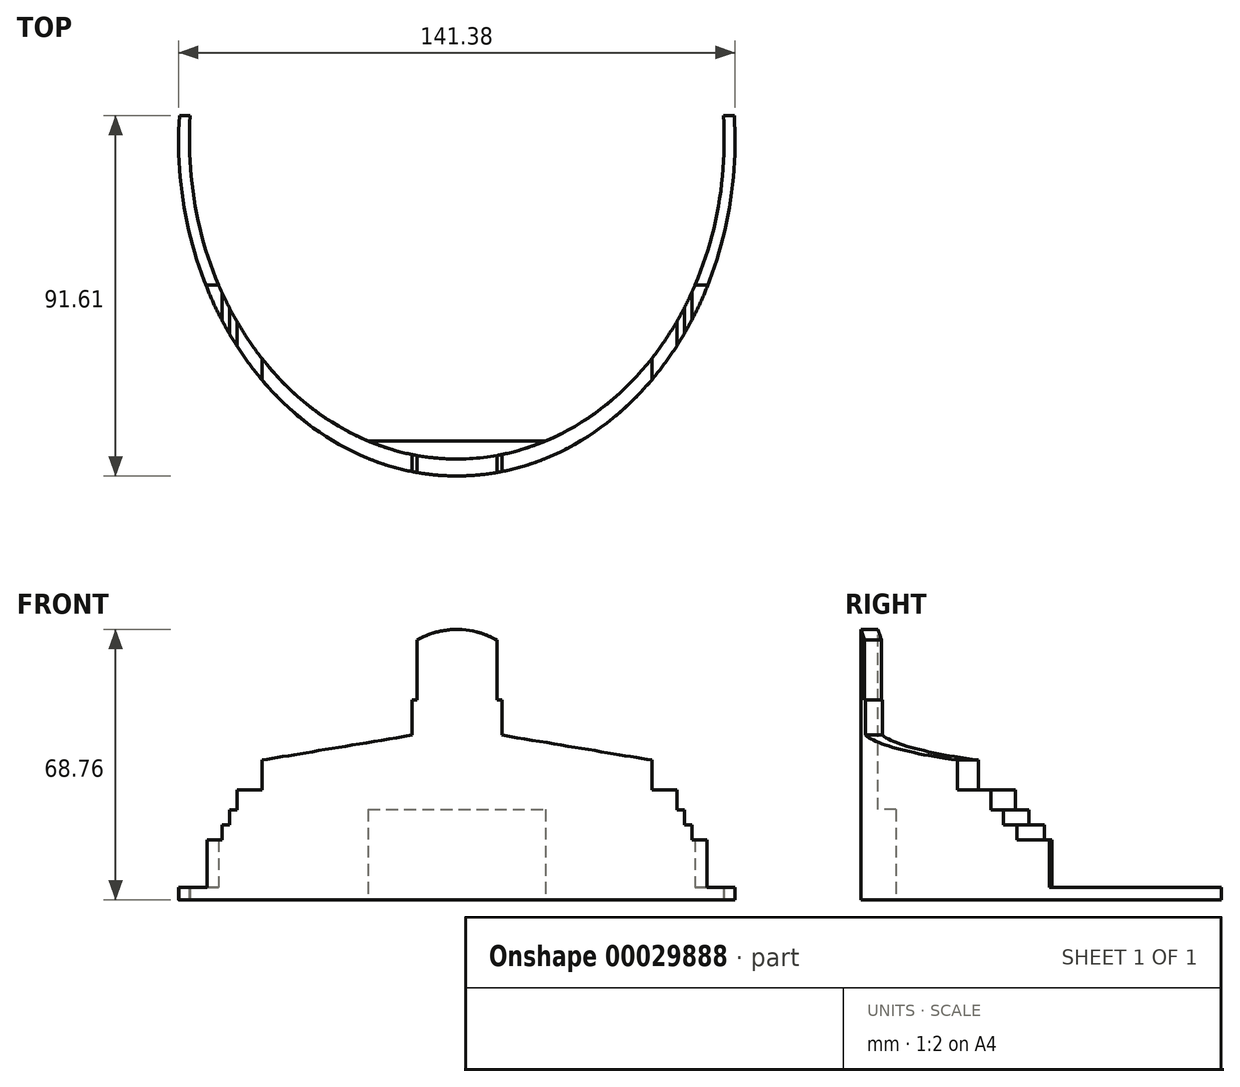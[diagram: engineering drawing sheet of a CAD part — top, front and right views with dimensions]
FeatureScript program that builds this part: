
annotation { "Feature Type Name" : "Feature", "Feature Type Description" : "" }
export const myFeature = defineFeature(function(context is Context, id is Id, definition is map)
    precondition{}
    {
        {
            var Q0;
            Q0=qCreatedBy(makeId("Front.planeOp"),FACE);
            var sketch = newSketch(context, id + "F0", { "sketchPlane" : qUnion([Q0])});
            skLineSegment(sketch, "E0", {"start": v(-63.5, 0) * mm, "end": v(63.5, 0) * mm});
            skLineSegment(sketch, "E1", {"start": v(63.5, 0) * mm, "end": v(63.5, 15.24) * mm});
            skLineSegment(sketch, "E2", {"start": v(63.5, 15.24) * mm, "end": v(59.69, 15.24) * mm});
            skLineSegment(sketch, "E3", {"start": v(59.69, 15.24) * mm, "end": v(59.69, 19.05) * mm});
            skLineSegment(sketch, "E4", {"start": v(59.69, 19.05) * mm, "end": v(57.78, 19.05) * mm});
            skLineSegment(sketch, "E5", {"start": v(57.78, 19.05) * mm, "end": v(57.78, 22.86) * mm});
            skLineSegment(sketch, "E6", {"start": v(57.78, 22.86) * mm, "end": v(55.88, 22.86) * mm});
            skLineSegment(sketch, "E7", {"start": v(55.88, 22.86) * mm, "end": v(55.88, 27.94) * mm});
            skLineSegment(sketch, "E8", {"start": v(55.88, 27.94) * mm, "end": v(49.53, 27.94) * mm});
            skLineSegment(sketch, "E9", {"start": v(49.53, 27.94) * mm, "end": v(49.53, 35.56) * mm});
            skLineSegment(sketch, "E10", {"start": v(49.53, 35.56) * mm, "end": v(11.43, 41.91) * mm});
            skLineSegment(sketch, "E11", {"start": v(11.43, 41.91) * mm, "end": v(11.43, 50.8) * mm});
            skLineSegment(sketch, "E12", {"start": v(11.43, 50.8) * mm, "end": v(10.16, 50.8) * mm});
            skLineSegment(sketch, "E13", {"start": v(10.16, 50.8) * mm, "end": v(10.16, 66.04) * mm});
            skLineSegment(sketch, "E14", {"start": v(10.16, 66.04) * mm, "end": v(0, 66.04) * mm, "construction": true});
            skLineSegment(sketch, "E15", {"start": v(0, 66.04) * mm, "end": v(0, 0) * mm, "construction": true});
            skLineSegment(sketch, "E16.MirrorCS", {"start": v(-10.16, 66.04) * mm, "end": v(0, 66.04) * mm, "construction": true});
            skLineSegment(sketch, "E17.MirrorCS", {"start": v(-10.16, 50.8) * mm, "end": v(-10.16, 66.04) * mm});
            skLineSegment(sketch, "E18.MirrorCS", {"start": v(-11.43, 41.91) * mm, "end": v(-11.43, 50.8) * mm});
            skLineSegment(sketch, "E19.MirrorCS", {"start": v(-49.53, 35.56) * mm, "end": v(-11.43, 41.91) * mm});
            skLineSegment(sketch, "E20.MirrorCS", {"start": v(-49.53, 27.94) * mm, "end": v(-49.53, 35.56) * mm});
            skLineSegment(sketch, "E21.MirrorCS", {"start": v(-55.88, 27.94) * mm, "end": v(-49.53, 27.94) * mm});
            skLineSegment(sketch, "E22.MirrorCS", {"start": v(-55.88, 22.86) * mm, "end": v(-55.88, 27.94) * mm});
            skLineSegment(sketch, "E23.MirrorCS", {"start": v(-57.78, 22.86) * mm, "end": v(-55.88, 22.86) * mm});
            skLineSegment(sketch, "E24.MirrorCS", {"start": v(-57.78, 19.05) * mm, "end": v(-57.79, 22.86) * mm});
            skLineSegment(sketch, "E25.MirrorCS", {"start": v(-59.69, 15.24) * mm, "end": v(-59.69, 19.05) * mm});
            skLineSegment(sketch, "E26.MirrorCS", {"start": v(-63.5, 15.24) * mm, "end": v(-59.69, 15.24) * mm});
            skLineSegment(sketch, "E27.MirrorCS", {"start": v(-63.5, 0) * mm, "end": v(-63.5, 15.24) * mm});
            skLineSegment(sketch, "E28", {"start": v(-59.69, 19.05) * mm, "end": v(-57.78, 19.05) * mm});
            skLineSegment(sketch, "E29", {"start": v(-10.16, 50.8) * mm, "end": v(-11.43, 50.8) * mm});
            skArc(sketch, "E30", {"start": v(10.16, 66.04) * mm, "mid": v(0, 68.76) * mm, "end": v(-10.16, 66.04) * mm});
            skSolve(sketch);
        }
        {
            var Q0;
            Q0=qCreatedBy(makeId("Top.planeOp"),FACE);
            var sketch = newSketch(context, id + "F1", { "sketchPlane" : qUnion([Q0])});
            skEllipse(sketch, "E31", {"center": v(0, 85.28) * mm, "majorRadius": 85.28 * mm, "minorRadius": 70.69 * mm, "majorAxis": v(0, -1)});
            skEllipse(sketch, "E32", {"center": v(0, 85.28) * mm, "majorRadius": 80.98 * mm, "minorRadius": 67.93 * mm, "majorAxis": v(0, -1)});
            skLineSegment(sketch, "E33", {"start": v(0, 0) * mm, "end": v(0, 170.56) * mm});
            skLineSegment(sketch, "E34", {"start": v(-70.5, 91.61) * mm, "end": v(70.5, 91.61) * mm});
            skSolve(sketch);
        }
        {
            var Q0;
            {var subQ3=sQuery(id+"F1.wireOp",EDGE,"E31");var subQ5=sQuery(id+"F1.wireOp",EDGE,"E33");var subQ7=makeQuery(id+"F1.imprint","INTERSECT",VERTEX,{"disambiguationData":[OD(0.0)],"derivedFrom":[subQ3,subQ5]});Q0=makeQuery(id+"F1.imprint","IMPRINT",FACE,{"disambiguationData":[TD([[makeQuery(id+"F1.imprint","IMPRINT",EDGE,{"disambiguationData":[TD([[subQ7,-1.0]])],"derivedFrom":subQ3}),1.0]])]});}
            var Q1;
            {var subQ3=sQuery(id+"F1.wireOp",EDGE,"E31");var subQ5=sQuery(id+"F1.wireOp",EDGE,"E33");var subQ7=makeQuery(id+"F1.imprint","INTERSECT",VERTEX,{"disambiguationData":[OD(0.0)],"derivedFrom":[subQ3,subQ5]});Q1=makeQuery(id+"F1.imprint","IMPRINT",FACE,{"disambiguationData":[TD([[makeQuery(id+"F1.imprint","IMPRINT",EDGE,{"disambiguationData":[TD([[subQ7,1.0]])],"derivedFrom":subQ3}),1.0]])]});}
            extrude(context, id + "F2", {"entities" : qUnion([Q0, Q1]), "depth" : 76.2 * mm});
        }
        {
            var Q0;
            Q0=qSketchRegion(id+"F0",true);
            extrude(context, id + "F3", {"entities" : qUnion([Q0]), "operationType" : NewBodyOperationType.INTERSECT, "oppositeDirection" : true, "depth" : 48.53 * mm});
        }
        {
            var Q0;
            Q0=qCreatedBy(makeId("Front.planeOp"),FACE);
            cPlane(context, id + "F4", {"entities" : qUnion([Q0]), "cplaneType" : CPlaneType.OFFSET, "offset" : 8.9 * mm, "oppositeDirection" : true, "width" : 152.4 * mm, "height" : 152.4 * mm});
        }
        {
            var Q0;
            Q0=qCreatedBy(id+"F4.planeOp",FACE);
            var sketch = newSketch(context, id + "F5", { "sketchPlane" : qUnion([Q0])});
            skLineSegment(sketch, "E35.bottom", {"start": v(-26.5, 0) * mm, "end": v(26.5, 0) * mm});
            skLineSegment(sketch, "E35.top", {"start": v(-26.5, 23) * mm, "end": v(26.5, 23) * mm});
            skLineSegment(sketch, "E35.left", {"start": v(-26.5, 0) * mm, "end": v(-26.5, 23) * mm});
            skLineSegment(sketch, "E35.right", {"start": v(26.5, 0) * mm, "end": v(26.5, 23) * mm});
            skSolve(sketch);
        }
        {
            var Q0;
            Q0=makeQuery(id+"F5.imprint","IMPRINT",FACE,{"disambiguationData":[TD([[makeQuery(id+"F5.imprint","IMPRINT",EDGE,{"derivedFrom":sQuery(id+"F5.wireOp",EDGE,"E35.bottom")}),1.0]])]});
            var Q1;
            Q1=makeQuery(id+"F2.opExtrude","SWEPT_FACE",FACE,{"disambiguationData":[OSD([sQuery(id+"F1.wireOp",EDGE,"E32")])]});
            extrude(context, id + "F6", {"entities" : qUnion([Q0]), "operationType" : NewBodyOperationType.ADD, "endBound" : BoundingType.UP_TO_SURFACE, "endBoundEntityFace" : qUnion([Q1]), "depth" : 25.4 * mm});
        }
        {
            var Q0;
            {var subQ3=sQuery(id+"F1.wireOp",EDGE,"E31");var subQ5=sQuery(id+"F1.wireOp",EDGE,"E33");var subQ7=makeQuery(id+"F1.imprint","INTERSECT",VERTEX,{"disambiguationData":[OD(0.0)],"derivedFrom":[subQ3,subQ5]});Q0=makeQuery(id+"F1.imprint","IMPRINT",FACE,{"disambiguationData":[TD([[makeQuery(id+"F1.imprint","IMPRINT",EDGE,{"disambiguationData":[TD([[subQ7,1.0]])],"derivedFrom":subQ3}),1.0]])]});}
            var Q1;
            {var subQ3=sQuery(id+"F1.wireOp",EDGE,"E31");var subQ5=sQuery(id+"F1.wireOp",EDGE,"E33");var subQ7=makeQuery(id+"F1.imprint","INTERSECT",VERTEX,{"disambiguationData":[OD(0.0)],"derivedFrom":[subQ3,subQ5]});Q1=makeQuery(id+"F1.imprint","IMPRINT",FACE,{"disambiguationData":[TD([[makeQuery(id+"F1.imprint","IMPRINT",EDGE,{"disambiguationData":[TD([[subQ7,-1.0]])],"derivedFrom":subQ3}),1.0]])]});}
            extrude(context, id + "F7", {"entities" : qUnion([Q0, Q1]), "operationType" : NewBodyOperationType.ADD, "depth" : 3.17 * mm});
        }
    });
